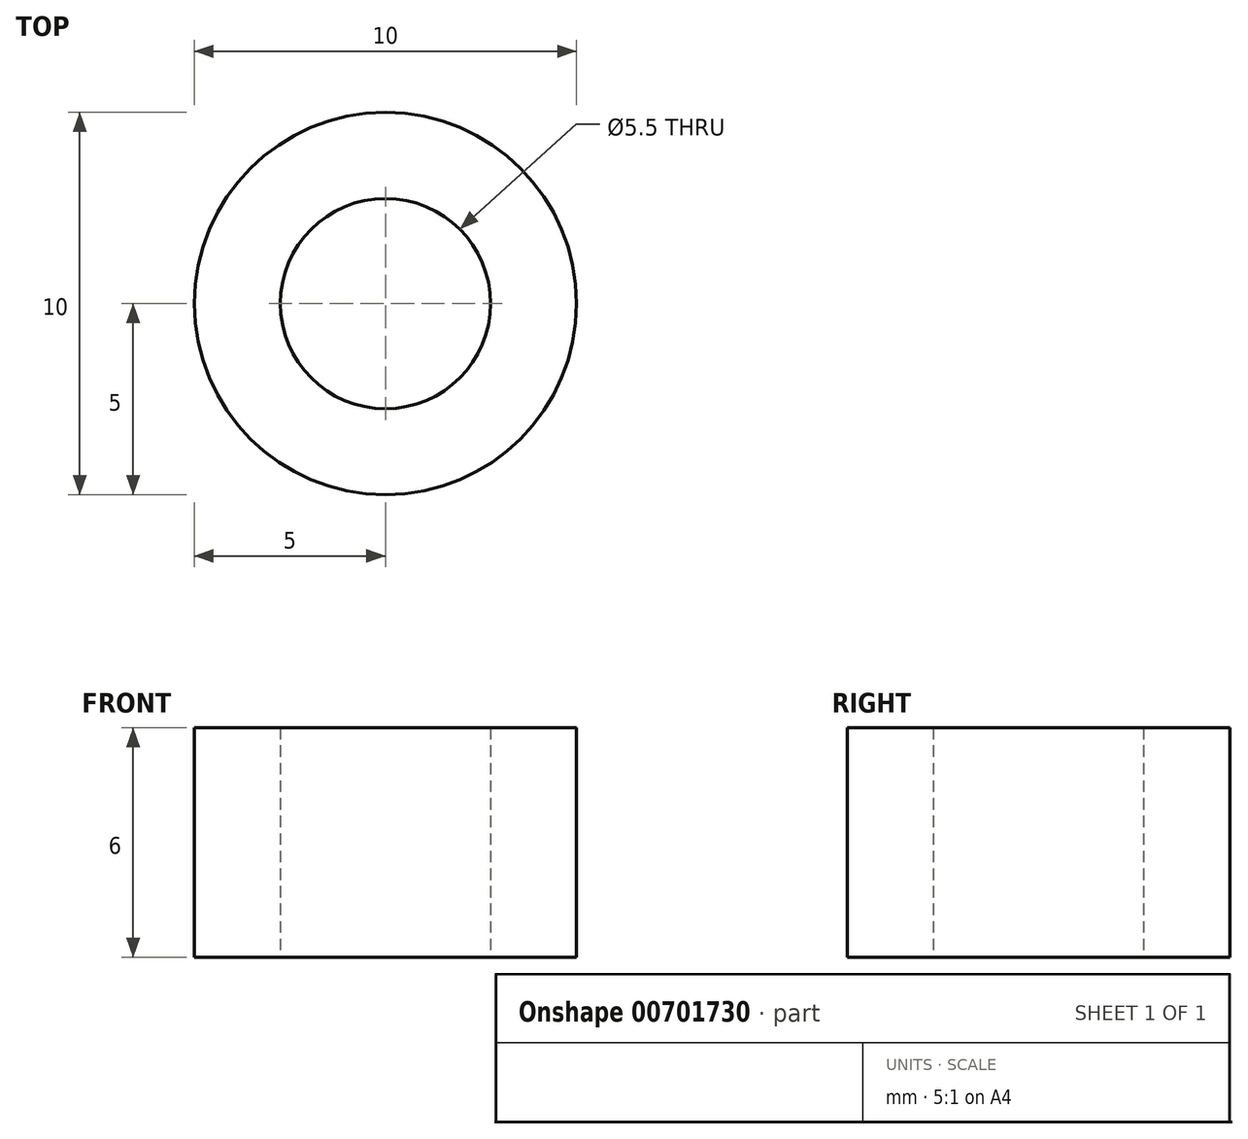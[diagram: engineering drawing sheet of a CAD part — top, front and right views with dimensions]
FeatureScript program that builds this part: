
annotation { "Feature Type Name" : "Feature", "Feature Type Description" : "" }
export const myFeature = defineFeature(function(context is Context, id is Id, definition is map)
    precondition{}
    {
        {
            var Q0;
            Q0=qCreatedBy(makeId("Top.planeOp"),FACE);
            var sketch = newSketch(context, id + "F0", { "sketchPlane" : qUnion([Q0])});
            skCircle(sketch, "E0", {"center": v(0, 0) * mm, "radius": 5 * mm});
            skCircle(sketch, "E1", {"center": v(0, 0) * mm, "radius": 2.75 * mm});
            skSolve(sketch);
        }
        {
            var Q0;
            Q0 = qSketchRegion(id + "F0", true);
            extrude(context, id + "F1", {"entities" : qUnion([Q0]), "depth" : 6 * mm, "offsetDistance" : 25 * mm});
        }
    });
